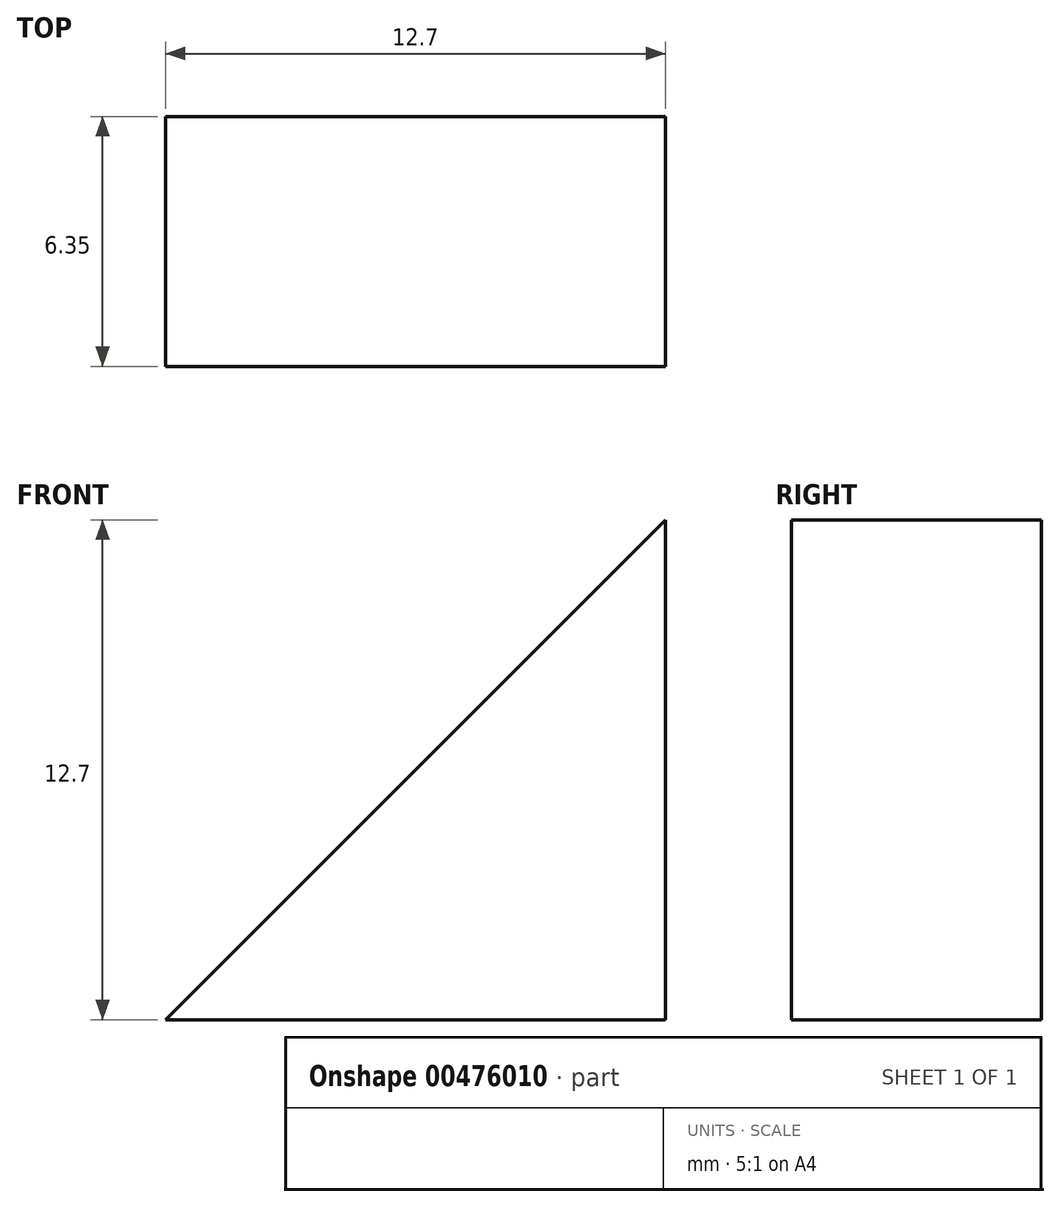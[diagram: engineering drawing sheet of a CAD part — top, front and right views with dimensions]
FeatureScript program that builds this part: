
annotation { "Feature Type Name" : "Feature", "Feature Type Description" : "" }
export const myFeature = defineFeature(function(context is Context, id is Id, definition is map)
    precondition{}
    {
        {
            var Q0;
            Q0=qCreatedBy(makeId("Front.planeOp"),FACE);
            var sketch = newSketch(context, id + "F0", { "sketchPlane" : qUnion([Q0])});
            skLineSegment(sketch, "E0", {"start": v(-12.7, 0) * mm, "end": v(0, 0) * mm});
            skLineSegment(sketch, "E1", {"start": v(0, 0) * mm, "end": v(0, 12.7) * mm});
            skLineSegment(sketch, "E2", {"start": v(0, 12.7) * mm, "end": v(-12.7, 0) * mm});
            skSolve(sketch);
        }
        {
            var Q0;
            Q0=makeQuery(id+"F0.imprint","IMPRINT",FACE,{"disambiguationData":[TD([[makeQuery(id+"F0.imprint","IMPRINT",EDGE,{"derivedFrom":sQuery(id+"F0.wireOp",EDGE,"E0")}),1.0]])]});
            extrude(context, id + "F1", {"entities" : qUnion([Q0]), "depth" : 6.35 * mm});
        }
    });
